# Revit family: 448733 SENTINEL KINETIC 200Z
name_source: partatom
category: Mechanical Equipment
revit_build: Autodesk Revit MEP 2013 (Build: 20120221_2030)
units: mm (PartAtom-declared; Revit-internal decimal feet)

## types (2) — shared parameters
AC Frequency Input = 50Hz nominal
AC Voltage Input = 220-240 V AC (single phase)
Category = Sentinel Kinetic
Condensate Pipe Diameter = 22 mm  [stored 0.0721785 ft]
Depth = 305 mm  [stored 1.00066 ft]
Family = Kinetic
Height (excluding Spigots) = 200 mm  [stored 0.656168 ft]
IP Rating = IP22
Length (excluding spigots) = 849 mm  [stored 2.78543 ft]
Length (including Spigots) = 895 mm  [stored 2.93635 ft]
Manufacturer - Name = Vent-Axia Ltd
Manufacturer - Website = www.vent-axia.com
Motor Rating = 150 Watts (max)
Operating Humidity = 0% to 95% RH
Operating Temperature = (-10C to +40C)
Operational and Maintenance Manual = http://www.vent-axia.com
Spigot Diameter = 125 mm  [stored 0.410105 ft]
Warranty period = Unit 2 Years , Motor 5 Years
Weight = 26kg
Width = 570 mm  [stored 1.87008 ft]

## per-type parameters (varying)
| type | Part Number | Product Description |
| 200Z | 448733 | Kinetic 200Z Horizontal |
| 200ZH | 449540 | Kinetic 200Z Horizontal with Humidity Sensor |

note: column(s) folded — value = type name in every type: Sub Type

note: [stored X ft] marks values corroborated as IEEE doubles in the binary element streams (Revit-internal decimal feet)

## geometry (parser evidence)
native form markers: Sweep x1
no freeform markers — native parametric forms only
